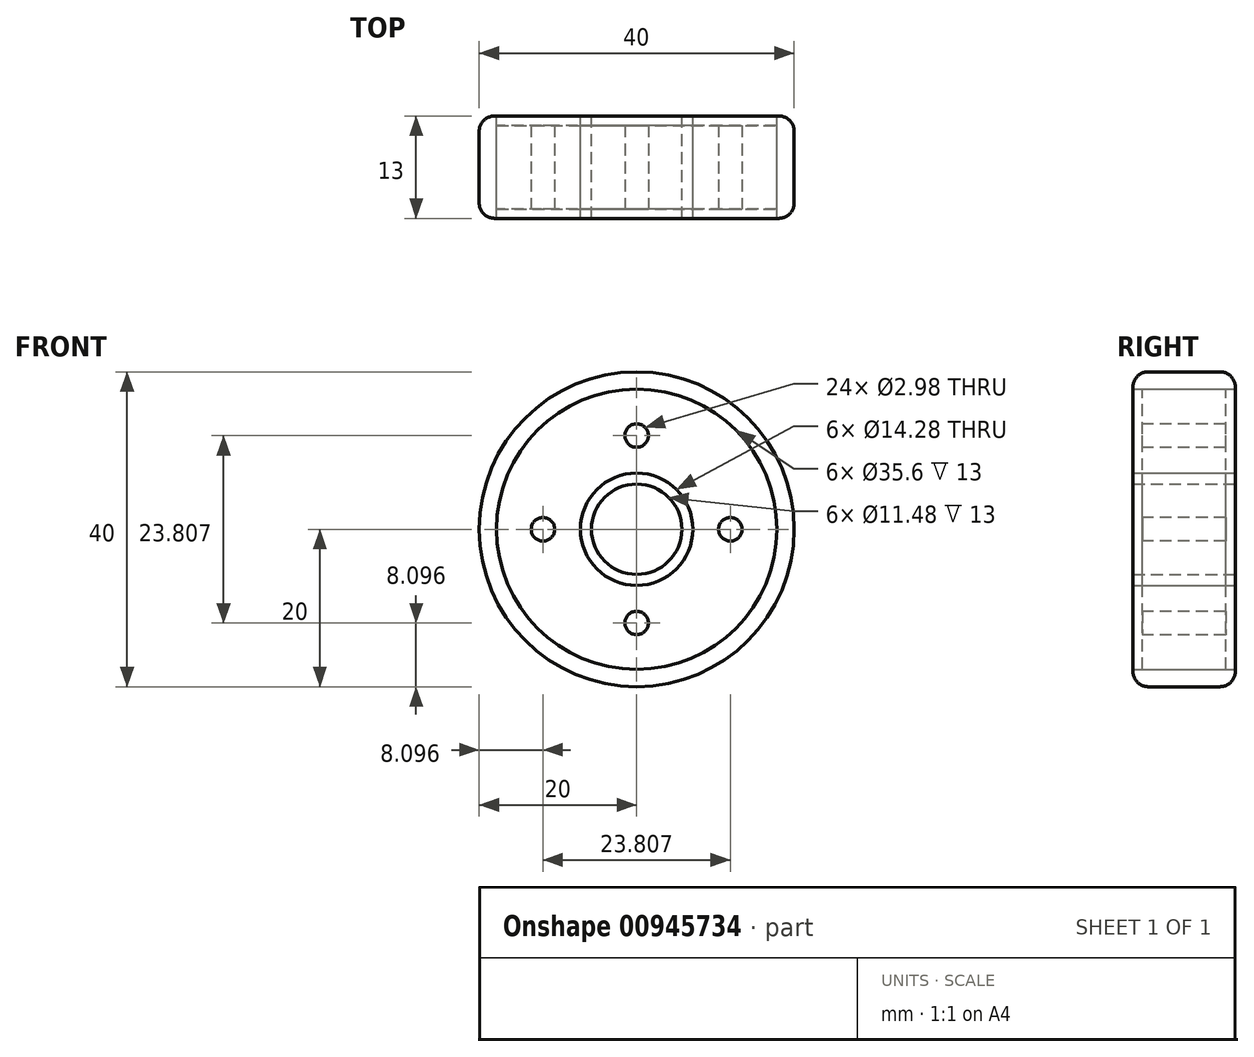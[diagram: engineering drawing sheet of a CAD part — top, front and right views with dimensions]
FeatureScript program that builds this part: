
annotation { "Feature Type Name" : "Feature", "Feature Type Description" : "" }
export const myFeature = defineFeature(function(context is Context, id is Id, definition is map)
    precondition{}
    {
        {
            var Q0;
            Q0=qCreatedBy(makeId("Front.planeOp"),FACE);
            var sketch = newSketch(context, id + "F0", { "sketchPlane" : qUnion([Q0])});
            skCircle(sketch, "E0", {"center": v(0, 0) * mm, "radius": 5.74 * mm});
            skCircle(sketch, "E1", {"center": v(0, 0) * mm, "radius": 20 * mm});
            skCircle(sketch, "E2.0", {"center": v(0, 0) * mm, "radius": 7.14 * mm});
            skCircle(sketch, "E3.0", {"center": v(0, 0) * mm, "radius": 17.8 * mm});
            skSolve(sketch);
        }
        {
            var Q0;
            Q0=makeQuery(id+"F0.imprint","IMPRINT",FACE,{"disambiguationData":[TD([[makeQuery(id+"F0.imprint","IMPRINT",EDGE,{"derivedFrom":sQuery(id+"F0.wireOp",EDGE,"E0")}),-1.0]])]});
            var Q1;
            Q1=makeQuery(id+"F0.imprint","IMPRINT",FACE,{"disambiguationData":[TD([[makeQuery(id+"F0.imprint","IMPRINT",EDGE,{"derivedFrom":sQuery(id+"F0.wireOp",EDGE,"E1")}),1.0]])]});
            extrude(context, id + "F1", {"entities" : qUnion([Q0, Q1]), "endBound" : BoundingType.SYMMETRIC, "depth" : 13 * mm, "offsetDistance" : 25 * mm});
        }
        {
            var Q0;
            Q0=makeQuery(id+"F0.imprint","IMPRINT",FACE,{"disambiguationData":[TD([[makeQuery(id+"F0.imprint","IMPRINT",EDGE,{"derivedFrom":sQuery(id+"F0.wireOp",EDGE,"E2.0")}),-1.0]])]});
            extrude(context, id + "F2", {"entities" : qUnion([Q0]), "endBound" : BoundingType.SYMMETRIC, "depth" : 10.6 * mm, "offsetDistance" : 25 * mm});
        }
        {
            var Q0;
            Q0=makeQuery(id+"F1.opExtrude","CAP_EDGE",EDGE,{"disambiguationData":[OSD([sQuery(id+"F0.wireOp",EDGE,"E1")])],"isStart":false});
            var Q1;
            Q1=makeQuery(id+"F1.opExtrude","CAP_EDGE",EDGE,{"disambiguationData":[OSD([sQuery(id+"F0.wireOp",EDGE,"E1")])],"isStart":true});
            fillet(context, id + "F3", {"entities" : qUnion([Q0, Q1]), "radius" : 1.93 * mm, "tangentPropagation" : true, "allowEdgeOverflow" : false});
        }
        {
            var Q0;
            Q0=makeQuery(id+"F1.opExtrude","CAP_FACE",FACE,{"disambiguationData":[OSD([sQuery(id+"F0.wireOp",EDGE,"E0"),sQuery(id+"F0.wireOp",EDGE,"E1")])],"isStart":false});
            var sketch = newSketch(context, id + "F4", { "sketchPlane" : qUnion([Q0])});
            skPoint(sketch, "E4", {"position": v(0, 11.9) * mm});
            skCircle(sketch, "E5", {"center": v(0, 11.9) * mm, "radius": 1.5 * mm});
            skPoint(sketch, "E6.orphan", {"position": v(0, 5.74) * mm});
            skPoint(sketch, "E7.orphan", {"position": v(0, 18.07) * mm});
            skSolve(sketch);
        }
        {
            var Q0;
            Q0=makeQuery(id+"F4.imprint","IMPRINT",FACE,{"disambiguationData":[TD([[makeQuery(id+"F4.imprint","IMPRINT",EDGE,{"derivedFrom":sQuery(id+"F4.wireOp",EDGE,"E5")}),1.0]])]});
            extrude(context, id + "F5", {"entities" : qUnion([Q0]), "operationType" : NewBodyOperationType.REMOVE, "endBound" : BoundingType.SYMMETRIC, "oppositeDirection" : true, "depth" : 25 * mm, "offsetDistance" : 25 * mm});
        }
        {
            var Q0;
            Q0=makeQuery(id+"F5.boolean.opBoolean","COPY",FACE,{"derivedFrom":makeQuery(id+"F5.opExtrude","SWEPT_FACE",FACE,{"disambiguationData":[OSD([sQuery(id+"F4.wireOp",EDGE,"E5")])]})});
            var Q1;
            Q1=makeQuery(id+"F1.opExtrude","SWEPT_FACE",FACE,{"disambiguationData":[OSD([sQuery(id+"F0.wireOp",EDGE,"E0")])]});
            circularPattern(context, id + "F6", {"patternType" : PatternType.FACE, "faces" : qUnion([Q0]), "axis" : qUnion([Q1]), "angle" : 360 * degree, "instanceCount" : 4, "equalSpace" : true});
        }
    });
